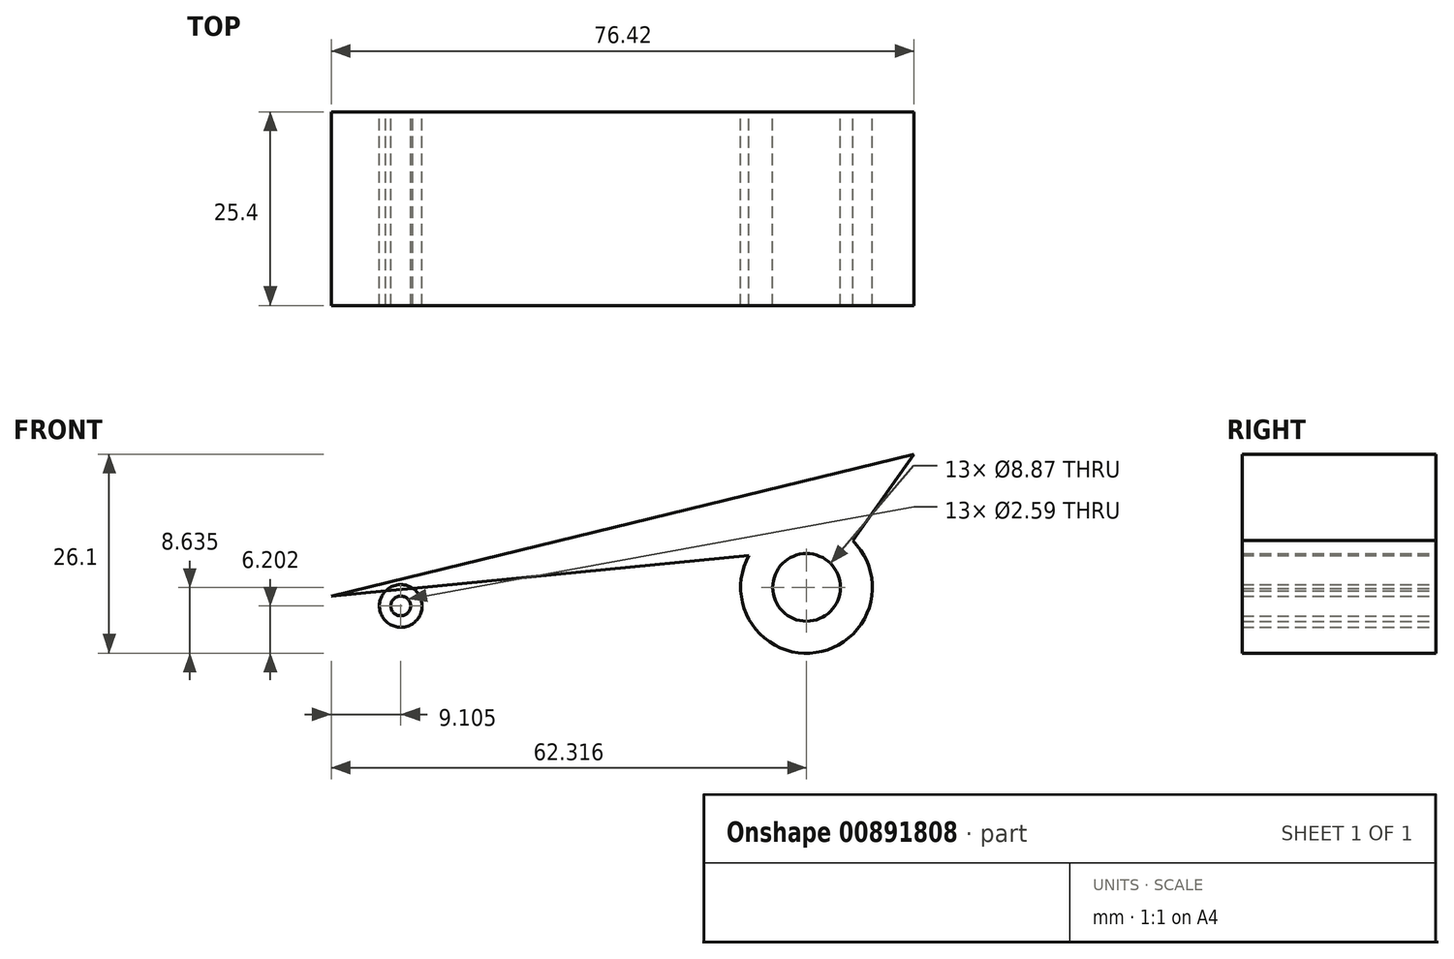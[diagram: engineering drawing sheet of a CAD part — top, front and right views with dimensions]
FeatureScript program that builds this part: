
annotation { "Feature Type Name" : "Feature", "Feature Type Description" : "" }
export const myFeature = defineFeature(function(context is Context, id is Id, definition is map)
    precondition{}
    {
        {
            var Q0;
            Q0=qCreatedBy(makeId("Front.planeOp"),FACE);
            var sketch = newSketch(context, id + "F0", { "sketchPlane" : qUnion([Q0])});
            skLineSegment(sketch, "E0", {"start": v(12.74, 12.87) * mm, "end": v(80.64, 19.53) * mm});
            skLineSegment(sketch, "E1", {"start": v(80.64, 19.53) * mm, "end": v(89.16, 31.5) * mm});
            skLineSegment(sketch, "E2", {"start": v(89.16, 31.5) * mm, "end": v(12.74, 12.87) * mm});
            skCircle(sketch, "E3", {"center": v(21.84, 11.61) * mm, "radius": 2.8 * mm});
            skCircle(sketch, "E4", {"center": v(21.84, 11.61) * mm, "radius": 1.3 * mm});
            skCircle(sketch, "E5", {"center": v(75.06, 14.04) * mm, "radius": 8.63 * mm});
            skCircle(sketch, "E6", {"center": v(75.06, 14.04) * mm, "radius": 4.43 * mm});
            skCircle(sketch, "E7", {"center": v(-21.18, 40.55) * mm, "radius": 1.3 * mm});
            skCircle(sketch, "E8", {"center": v(-21.6, 56.88) * mm, "radius": 4.43 * mm});
            skSolve(sketch);
        }
        {
            var Q0;
            {var subQ0=sQuery(id+"F0.wireOp",EDGE,"E2");Q0=makeQuery(id+"F0.imprint","IMPRINT",FACE,{"disambiguationData":[TD([[makeQuery(id+"F0.imprint","IMPRINT",EDGE,{"derivedFrom":subQ0}),1.0]])]});}
            var Q1;
            Q1=makeQuery(id+"F0.imprint","IMPRINT",FACE,{"disambiguationData":[TD([[makeQuery(id+"F0.imprint","IMPRINT",EDGE,{"derivedFrom":sQuery(id+"F0.wireOp",EDGE,"E6")}),-1.0]])]});
            var Q2;
            {var subQ0=sQuery(id+"F0.wireOp",EDGE,"E1");var subQ1=sQuery(id+"F0.wireOp",EDGE,"E0");var subQ2=makeQuery(id+"F0.imprint","INTERSECT",VERTEX,{"derivedFrom":[subQ1,subQ0]});Q2=makeQuery(id+"F0.imprint","IMPRINT",FACE,{"disambiguationData":[TD([[makeQuery(id+"F0.imprint","IMPRINT",EDGE,{"disambiguationData":[TD([[subQ2,1.0]])],"derivedFrom":subQ1}),1.0]])]});}
            var Q3;
            Q3=makeQuery(id+"F0.imprint","IMPRINT",FACE,{"disambiguationData":[TD([[makeQuery(id+"F0.imprint","IMPRINT",EDGE,{"derivedFrom":sQuery(id+"F0.wireOp",EDGE,"E4")}),-1.0]])]});
            var Q4;
            {var subQ0=sQuery(id+"F0.wireOp",EDGE,"E3");var subQ1=sQuery(id+"F0.wireOp",EDGE,"E0");var subQ2=makeQuery(id+"F0.imprint","INTERSECT",VERTEX,{"disambiguationData":[OD(0.0)],"derivedFrom":[subQ1,subQ0]});Q4=makeQuery(id+"F0.imprint","IMPRINT",FACE,{"disambiguationData":[TD([[makeQuery(id+"F0.imprint","IMPRINT",EDGE,{"disambiguationData":[TD([[subQ2,-1.0]])],"derivedFrom":subQ1}),1.0]])]});}
            extrude(context, id + "F1", {"entities" : qUnion([Q0, Q1, Q2, Q3, Q4]), "depth" : 25.4 * mm, "offsetDistance" : 25.4 * mm});
        }
    });
